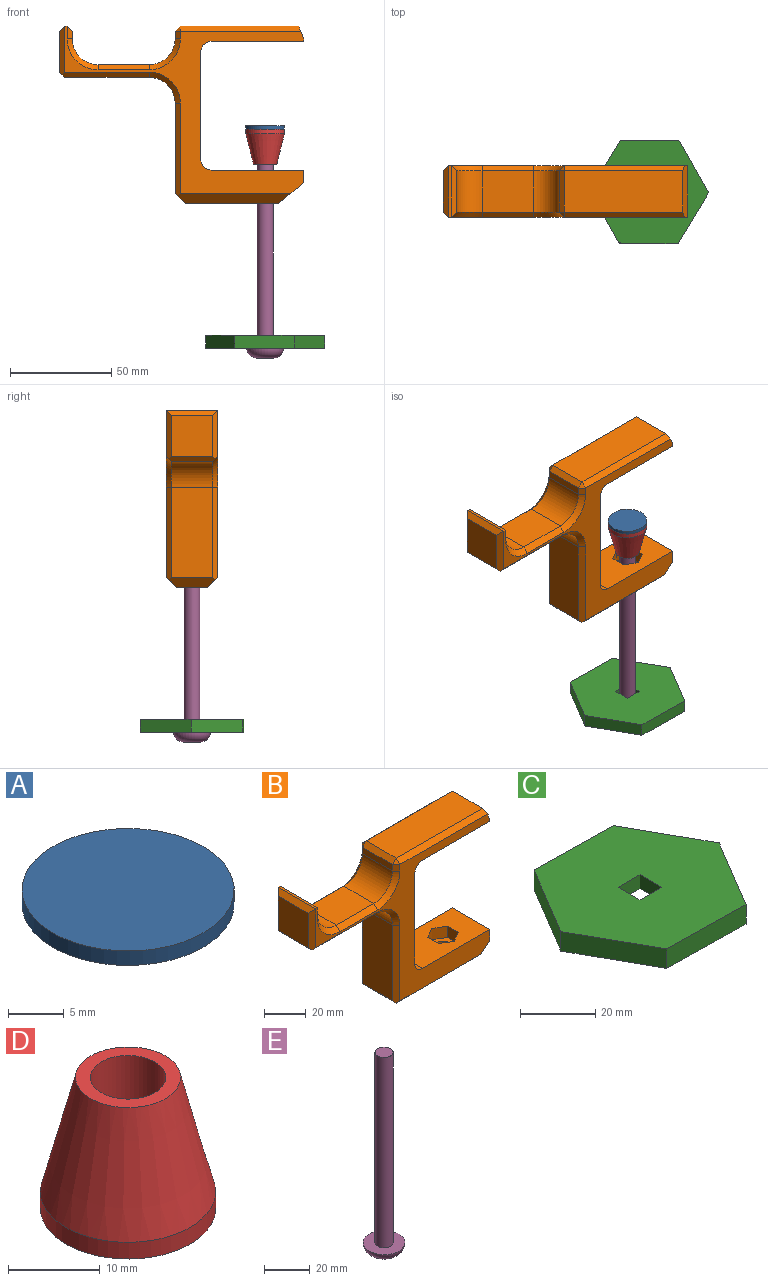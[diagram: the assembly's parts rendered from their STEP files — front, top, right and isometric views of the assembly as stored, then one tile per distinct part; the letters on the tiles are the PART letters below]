
ASSEMBLY  parts=5 mates=3
PART A: 3 faces, bbox 19.1x19.1x1.6 mm
  f0: cylinder r=9.53mm len=19.05mm, axis (0,0,1), area 95mm2, adj f1,f2
  f1: plane 19.05x19.05mm, normal (0,0,-1), area 285mm2, adj f0
  f2: plane 19.05x19.05mm, normal (0,0,1), area 285mm2, adj f0
PART B: 67 faces, bbox 120.7x25.4x87.6 mm
  f0: plane 45.72x15.24mm, normal (0,0,-1), area 552.4mm2, adj f1,f48,f49,f50,f59,f60,f62,f63
  f1: plane 25.4x12.7mm, normal (0.62,0,-0.78), area 370.6mm2, adj f0,f5,f15,f16,f48,f50,f60,f61
  f2: plane 45.72x25.4mm, normal (0,0,1), area 1016mm2, adj f5,f15,f16,f46,f52,f53,f54,f55
  f3: plane 41.91x20.32mm, normal (0,0,-1), area 851.6mm2, adj f38,f39,f42,f45
  f4: plane 44.45x20.32mm, normal (-1,0,0), area 903.2mm2, adj f39,f40,f43,f49
  f5: plane 25.4x6.35mm, normal (1,0,0), area 161.3mm2, adj f1,f2,f15,f16
  f6: plane 53.34x25.4mm, normal (1,0,0), area 1354.8mm2, adj f15,f16,f46,f47
  f7: plane 45.72x25.4mm, normal (0,0,-1), area 1161.3mm2, adj f8,f15,f16,f47
  f8: plane 25.4x1.27mm, normal (1,0,0), area 32.3mm2, adj f7,f15,f16,f51
  f9: plane 58.42x20.32mm, normal (0,0,1), area 1187.1mm2, adj f25,f29,f30,f51
  f10: plane 20.32x3.81mm, normal (-1,0,0), area 77.4mm2, adj f18,f24,f29,f34
  f11: plane 25.4x20.32mm, normal (0,0,1), area 516.1mm2, adj f17,f18,f20,f31
  f12: plane 20.32x3.81mm, normal (1,0,0), area 77.4mm2, adj f17,f21,f23,f26
  f13: plane 25.4x1.27mm, normal (0,0,1), area 32.3mm2, adj f15,f16,f23,f35
  f14: plane 20.32x20.32mm, normal (-1,0,0), area 412.9mm2, adj f35,f36,f37,f38
  f15: plane 118.11x82.55mm, normal (0,-1,0), area 1893.2mm2, adj f1,f2,f5,f6,f7,f8,f13,f26
  f16: plane 118.11x82.55mm, normal (0,1,0), area 1893.2mm2, adj f1,f2,f5,f6,f7,f8,f13,f19
  f17: cylinder r=12.7mm len=20.32mm, axis (0,-1,0), area 405.4mm2, adj f11,f12,f19,f28
  f18: cylinder r=12.7mm len=20.32mm, axis (0,-1,0), area 405.4mm2, adj f10,f11,f22,f33
  f19: cone r=15.24mm half-angle=45deg, axis (0,1,0), area 78.8mm2, adj f16,f17,f20,f21
  f20: plane 25.4x2.54mm, normal (0,0.71,0.71), area 91.2mm2, adj f11,f16,f19,f22
  f21: plane 6.35x2.54mm, normal (0.71,0.71,0), area 18.2mm2, adj f12,f16,f19,f23
  f22: cone r=15.24mm half-angle=45deg, axis (0,1,0), area 78.8mm2, adj f16,f18,f20,f24
  f23: plane 25.4x2.54mm, normal (0.71,0,0.71), area 82.1mm2, adj f12,f13,f21,f26
  f24: plane 3.81x2.54mm, normal (-0.71,0.71,0), area 13.7mm2, adj f10,f16,f22,f27
  f25: plane 59.44x2.54mm, normal (0,0.71,0.71), area 211.7mm2, adj f9,f16,f27,f51
  f26: plane 6.35x2.54mm, normal (0.71,-0.71,0), area 18.2mm2, adj f12,f15,f23,f28
  f27: plane 2.54x2.54mm, normal (-0.58,0.58,0.58), area 5.6mm2, adj f24,f25,f29
  f28: cone r=15.24mm half-angle=45deg, axis (0,-1,0), area 78.8mm2, adj f15,f17,f26,f31
  f29: plane 20.32x2.54mm, normal (-0.71,0,0.71), area 73mm2, adj f9,f10,f27,f32
  f30: plane 59.44x2.54mm, normal (0,-0.71,0.71), area 211.7mm2, adj f9,f15,f32,f51
  f31: plane 25.4x2.54mm, normal (0,-0.71,0.71), area 91.2mm2, adj f11,f15,f28,f33
  f32: plane 2.54x2.54mm, normal (-0.58,-0.58,0.58), area 5.6mm2, adj f29,f30,f34
  f33: cone r=15.24mm half-angle=45deg, axis (0,-1,0), area 78.8mm2, adj f15,f18,f31,f34
  f34: plane 3.81x2.54mm, normal (-0.71,-0.71,0), area 13.7mm2, adj f10,f15,f32,f33
  f35: plane 25.4x2.54mm, normal (-0.71,0,0.71), area 82.1mm2, adj f13,f14,f36,f37
  f36: plane 24.13x2.54mm, normal (-0.71,-0.71,0), area 79.8mm2, adj f14,f15,f35,f38,f45
  f37: plane 24.13x2.54mm, normal (-0.71,0.71,0), area 79.8mm2, adj f14,f16,f35,f38,f42
  f38: plane 22.86x2.54mm, normal (-0.71,0,-0.71), area 77.6mm2, adj f3,f14,f36,f37,f42,f45
  f39: cylinder r=12.7mm len=20.32mm, axis (0,1,0), area 405.4mm2, adj f3,f4,f41,f44
  f40: plane 45.72x2.54mm, normal (-0.71,0.71,0), area 161.9mm2, adj f4,f16,f41,f48,f49
  f41: cone r=15.24mm half-angle=45deg, axis (0,1,0), area 78.8mm2, adj f16,f39,f40,f42
  f42: plane 43.18x2.54mm, normal (0,0.71,-0.71), area 152.8mm2, adj f3,f16,f37,f38,f41
  f43: plane 45.72x2.54mm, normal (-0.71,-0.71,0), area 161.9mm2, adj f4,f15,f44,f49,f50
  f44: cone r=15.24mm half-angle=45deg, axis (0,-1,0), area 78.8mm2, adj f15,f39,f43,f45
  f45: plane 43.18x2.54mm, normal (0,-0.71,-0.71), area 152.8mm2, adj f3,f15,f36,f38,f44
  f46: cylinder r=5.08mm len=25.4mm, axis (0,-1,0), area 202.7mm2, adj f2,f6,f15,f16
  f47: cylinder r=5.08mm len=25.4mm, axis (0,1,0), area 202.7mm2, adj f6,f7,f15,f16
  f48: plane 55.88x5.08mm, normal (0,0.71,-0.71), area 367.2mm2, adj f0,f1,f16,f40,f49
  f49: plane 22.86x5.08mm, normal (-0.71,0,-0.71), area 141.4mm2, adj f0,f4,f40,f43,f48,f50
  f50: plane 55.88x5.08mm, normal (0,-0.71,-0.71), area 367.2mm2, adj f0,f1,f15,f43,f49
  f51: plane 25.4x6.35mm, normal (0.93,0,0.37), area 166.8mm2, adj f8,f9,f15,f16,f25,f30
  f52: plane 6.6x6.48mm, normal (0.5,0.87,0), area 49.4mm2, adj f2,f53,f57,f58
  f53: plane 6.6x6.48mm, normal (-0.5,0.87,0), area 49.4mm2, adj f2,f52,f54,f58
  f54: plane 7.48x6.6mm, normal (-1,0,0), area 49.4mm2, adj f2,f53,f55,f58
  f55: plane 6.6x6.48mm, normal (-0.5,-0.87,0), area 49.4mm2, adj f2,f54,f56,f58
  f56: plane 6.6x6.48mm, normal (0.5,-0.87,0), area 49.4mm2, adj f2,f55,f57,f58
  f57: plane 7.48x6.6mm, normal (1,0,0), area 49.4mm2, adj f2,f52,f56,f58
  f58: plane 14.96x12.95mm, normal (0,0,1), area 93.4mm2, adj f52,f53,f54,f55,f56,f57,f66
  f59: plane 6.6x6.48mm, normal (0.5,0.87,0), area 49.4mm2, adj f0,f60,f64,f65
  f60: plane 6.6x6.48mm, normal (-0.5,0.87,0), area 49.4mm2, adj f0,f1,f59,f61,f65
  f61: plane 7.48x6.5mm, normal (-1,0,0), area 48.6mm2, adj f1,f60,f62,f65
  f62: plane 6.6x6.48mm, normal (-0.5,-0.87,0), area 49.4mm2, adj f0,f1,f61,f63,f65
  f63: plane 6.6x6.48mm, normal (0.5,-0.87,0), area 49.4mm2, adj f0,f62,f64,f65
  f64: plane 7.48x6.6mm, normal (1,0,0), area 49.4mm2, adj f0,f59,f63,f65
  f65: plane 14.96x12.95mm, normal (0,0,-1), area 93.4mm2, adj f59,f60,f61,f62,f63,f64,f66
  f66: cylinder r=4.06mm len=8.13mm, axis (0,0,1), area 84.3mm2, adj f58,f65
PART C: 14 faces, bbox 58.7x51.2x6.4 mm
  f0: plane 8.18x4.57mm, normal (-1,0,0), area 37.4mm2, adj f1,f9,f10,f13
  f1: plane 8.18x4.57mm, normal (0,1,0), area 37.4mm2, adj f0,f2,f10,f13
  f2: plane 8.18x4.57mm, normal (1,0,0), area 37.4mm2, adj f1,f9,f10,f13
  f3: plane 29.33x6.35mm, normal (-0.02,-1,0), area 186.2mm2, adj f4,f8,f10,f11
  f4: plane 25.17x15.06mm, normal (0.86,-0.51,0), area 186.2mm2, adj f3,f5,f10,f11
  f5: plane 25.63x14.27mm, normal (0.87,0.49,0), area 186.2mm2, adj f4,f6,f10,f11
  f6: plane 29.33x6.35mm, normal (0.02,1,0), area 186.2mm2, adj f5,f7,f10,f11
  f7: plane 25.17x15.06mm, normal (-0.86,0.51,0), area 186.2mm2, adj f6,f8,f10,f11
  f8: plane 25.63x14.27mm, normal (-0.87,-0.49,0), area 186.2mm2, adj f3,f7,f10,f11
  f9: plane 8.18x4.57mm, normal (0,-1,0), area 37.4mm2, adj f0,f2,f10,f13
  f10: plane 58.65x51.25mm, normal (0,0,1), area 2168mm2, adj f0,f1,f2,f3,f4,f5,f6,f7
  f11: plane 58.65x51.25mm, normal (0,0,-1), area 1964.9mm2, adj f3,f4,f5,f6,f7,f8,f12
  f12: cylinder r=9.27mm len=18.54mm, axis (0,0,-1), area 103.6mm2, adj f11,f13
  f13: plane 18.54x18.54mm, normal (0,0,-1), area 203.1mm2, adj f0,f1,f2,f9,f12
PART D: 6 faces, bbox 19.1x19.1x17.5 mm
  f0: cylinder r=9.53mm len=19.05mm, axis (0,0,1), area 133mm2, adj f1,f5
  f1: plane 19.05x19.05mm, normal (0,0,-1), area 285mm2, adj f0
  f2: plane 11.43x11.43mm, normal (0,0,1), area 49.7mm2, adj f3,f5
  f3: cylinder r=4.1mm len=9.53mm, axis (0,0,1), area 245.5mm2, adj f2,f4
  f4: cone r=0mm half-angle=59deg, axis (0,0,1), area 61.7mm2, adj f3
  f5: cone r=5.71mm half-angle=14deg, axis (0,0,-1), area 752.1mm2, adj f0,f2
PART E: 5 faces, bbox 18.3x18.3x106.4 mm
  f0: plane 8.15x8.15mm, normal (0,0,-1), area 52.1mm2, adj f4
  f1: plane 18.29x18.29mm, normal (0,0,1), area 214mm2, adj f2,f4
  f2: cylinder r=3.94mm len=101.6mm, axis (0,0,-1), area 2513.3mm2, adj f1,f3
  f3: plane 7.87x7.87mm, normal (0,0,1), area 48.7mm2, adj f2
  f4: torus R=4.07mm, axis (0,0,-1), area 348.1mm2, adj f0,f1
PLACE A rot(axis=(0,1,0),180deg) t=(65.21,95.51,96.7)mm
PLACE B rot(axis=(0,0,-1),0deg) t=(33.46,108.21,120.5)mm fixed
PLACE C rot(axis=(0,0,-1),0deg) t=(65.21,95.51,5.86)mm
PLACE D rot(axis=(0,1,0),180deg) t=(65.21,95.51,96.7)mm
PLACE E t=(65.21,95.51,5.86)mm
MATE slider B.f66 <-> A.f0  axis (0,0,-1) through (65.21,95.51,84)mm
MATE fastened E.f2 <-> D.f0  axis (0,0,1) through (65.21,95.51,107.46)mm
MATE fastened C.f12 <-> E.f2  axis (0,0,-1) through (65.21,95.51,5.86)mm
